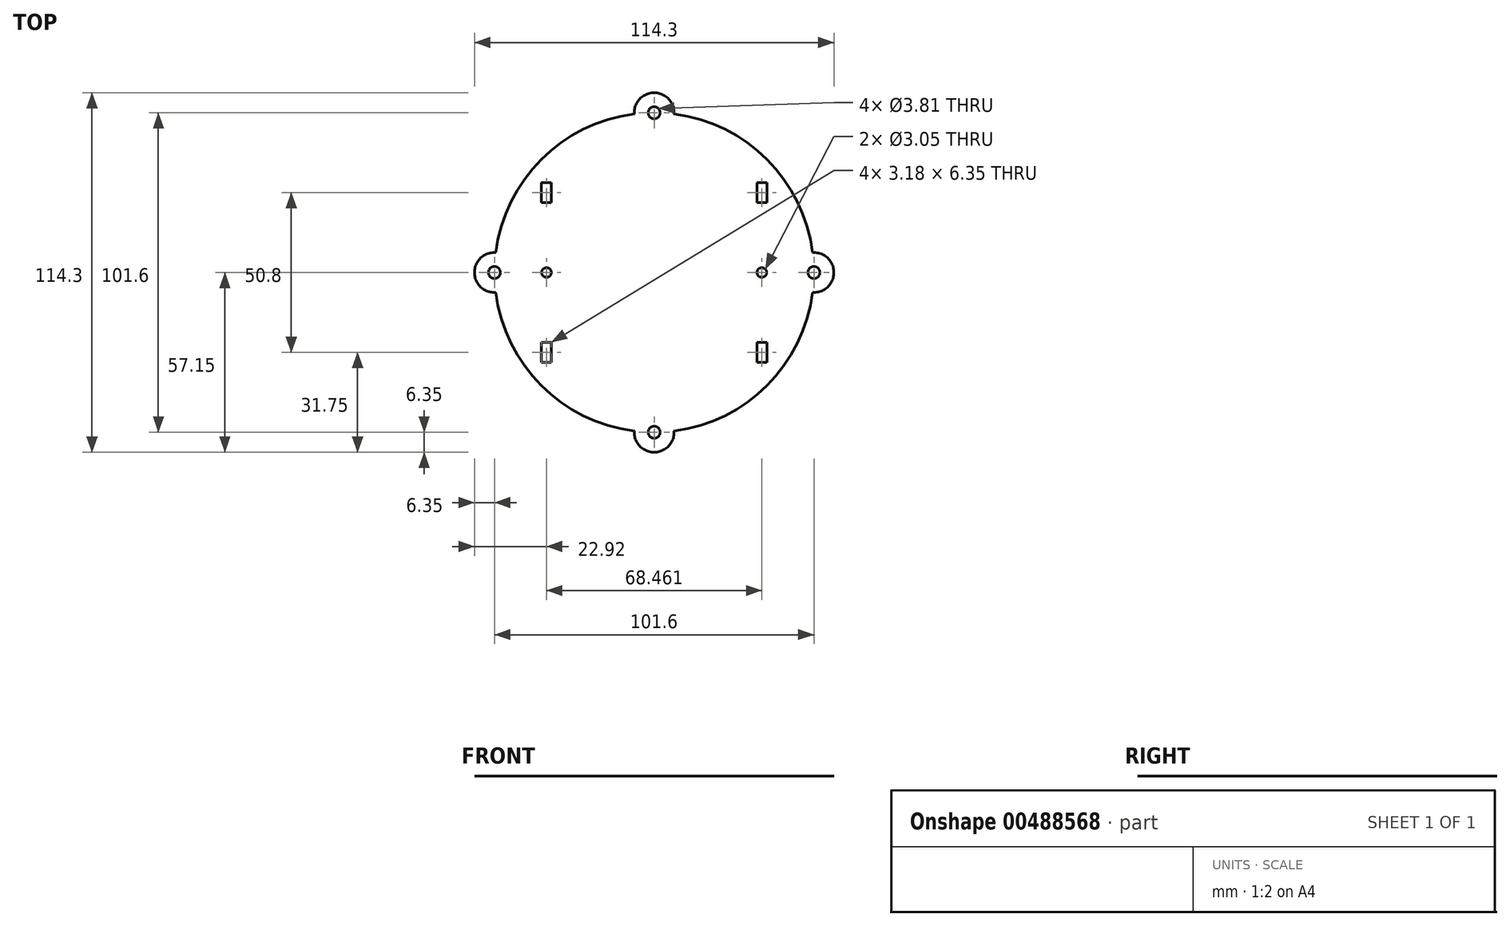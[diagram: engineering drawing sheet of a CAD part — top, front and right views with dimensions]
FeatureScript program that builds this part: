
annotation { "Feature Type Name" : "Feature", "Feature Type Description" : "" }
export const myFeature = defineFeature(function(context is Context, id is Id, definition is map)
    precondition{}
    {
        {
            var Q0;
            Q0=qCreatedBy(makeId("Top.planeOp"),FACE);
            var sketch = newSketch(context, id + "F0", { "sketchPlane" : qUnion([Q0])});
            skArc(sketch, "E0", {"start": v(-50.4, -6.34) * mm, "mid": v(-35.92, -35.92) * mm, "end": v(-6.34, -50.4) * mm});
            skArc(sketch, "E1", {"start": v(6.34, 50.4) * mm, "mid": v(0, 57.15) * mm, "end": v(-6.34, 50.4) * mm});
            skArc(sketch, "E2", {"start": v(50.4, -6.34) * mm, "mid": v(57.15, 0) * mm, "end": v(50.4, 6.34) * mm});
            skArc(sketch, "E3", {"start": v(-6.34, -50.4) * mm, "mid": v(0, -57.15) * mm, "end": v(6.34, -50.4) * mm});
            skArc(sketch, "E4", {"start": v(-50.4, 6.34) * mm, "mid": v(-57.15, 0) * mm, "end": v(-50.4, -6.34) * mm});
            skArc(sketch, "E5.trimOffspring", {"start": v(-6.34, 50.4) * mm, "mid": v(-35.92, 35.92) * mm, "end": v(-50.4, 6.34) * mm});
            skArc(sketch, "E6.trimOffspring", {"start": v(50.4, 6.34) * mm, "mid": v(35.92, 35.92) * mm, "end": v(6.34, 50.4) * mm});
            skArc(sketch, "E7.trimOffspring", {"start": v(6.34, -50.4) * mm, "mid": v(35.92, -35.92) * mm, "end": v(50.4, -6.34) * mm});
            skCircle(sketch, "E8", {"center": v(-50.8, 0) * mm, "radius": 1.9 * mm});
            skCircle(sketch, "E9", {"center": v(0, 50.8) * mm, "radius": 1.9 * mm});
            skCircle(sketch, "E10", {"center": v(50.8, 0) * mm, "radius": 1.9 * mm});
            skCircle(sketch, "E11", {"center": v(0, -50.8) * mm, "radius": 1.9 * mm});
            skLineSegment(sketch, "E12", {"start": v(0, 0) * mm, "end": v(34.23, 0) * mm, "construction": true});
            skLineSegment(sketch, "E13", {"start": v(34.23, 0) * mm, "end": v(34.23, 25.4) * mm, "construction": true});
            skLineSegment(sketch, "E14.bottom", {"start": v(35.82, 22.23) * mm, "end": v(32.64, 22.23) * mm});
            skLineSegment(sketch, "E14.top", {"start": v(35.82, 28.58) * mm, "end": v(32.64, 28.58) * mm});
            skLineSegment(sketch, "E14.left", {"start": v(35.82, 22.23) * mm, "end": v(35.82, 28.58) * mm});
            skLineSegment(sketch, "E14.right", {"start": v(32.64, 22.23) * mm, "end": v(32.64, 28.58) * mm});
            skPoint(sketch, "E14.middle", {"position": v(34.23, 25.4) * mm});
            skLineSegment(sketch, "E15.MirrorCS", {"start": v(32.64, -22.23) * mm, "end": v(32.64, -28.58) * mm});
            skLineSegment(sketch, "E16.MirrorCS", {"start": v(35.82, -28.58) * mm, "end": v(32.64, -28.58) * mm});
            skLineSegment(sketch, "E17.MirrorCS", {"start": v(35.82, -22.23) * mm, "end": v(35.82, -28.58) * mm});
            skLineSegment(sketch, "E18.MirrorCS", {"start": v(35.82, -22.23) * mm, "end": v(32.64, -22.23) * mm});
            skLineSegment(sketch, "E19.MirrorCS", {"start": v(-35.82, 28.58) * mm, "end": v(-32.64, 28.58) * mm});
            skLineSegment(sketch, "E20.MirrorCS", {"start": v(-32.64, 22.23) * mm, "end": v(-32.64, 28.58) * mm});
            skLineSegment(sketch, "E21.MirrorCS", {"start": v(-35.82, 22.23) * mm, "end": v(-32.64, 22.23) * mm});
            skLineSegment(sketch, "E22.MirrorCS", {"start": v(-35.82, 22.23) * mm, "end": v(-35.82, 28.58) * mm});
            skLineSegment(sketch, "E23.MirrorCS", {"start": v(-35.82, -22.23) * mm, "end": v(-32.64, -22.23) * mm});
            skLineSegment(sketch, "E24.MirrorCS", {"start": v(-32.64, -22.23) * mm, "end": v(-32.64, -28.58) * mm});
            skLineSegment(sketch, "E25.MirrorCS", {"start": v(-35.82, -28.58) * mm, "end": v(-32.64, -28.58) * mm});
            skLineSegment(sketch, "E26.MirrorCS", {"start": v(-35.82, -22.23) * mm, "end": v(-35.82, -28.58) * mm});
            skCircle(sketch, "E27", {"center": v(34.23, 0) * mm, "radius": 1.52 * mm});
            skCircle(sketch, "E28.MirrorC", {"center": v(-34.23, 0) * mm, "radius": 1.52 * mm});
            skSolve(sketch);
        }
        {
            var Q0;
            Q0=makeQuery(id+"F0.imprint","IMPRINT",FACE,{"disambiguationData":[TD([[makeQuery(id+"F0.imprint","IMPRINT",EDGE,{"derivedFrom":sQuery(id+"F0.wireOp",EDGE,"E0")}),1.0]])]});
            extrude(context, id + "F1", {"entities" : qUnion([Q0]), "depth" : 1 / 203.2 * mm});
        }
    });
